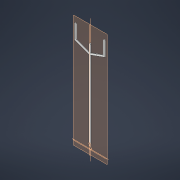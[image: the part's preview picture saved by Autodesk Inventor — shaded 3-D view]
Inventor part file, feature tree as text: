
AUTODESK INVENTOR PART (.ipt)
format: ipt  version: 2021 (Build 250183000, 183)  size: 134,656 bytes
history: native  units: mm
features: extrude x2, sketch x2, mirror x1, plane x1
ambient origin geometry x8: Origin, YZ Plane, XZ Plane, XY Plane, X Axis, Y Axis, Z Axis, Center Point
bodies: Solid1 (feature_tree)
feature tree (6):
  extrude  "Extrusion1"  Depth=4.0mm
  mirror  "Mirror1"
  plane  "Work Plane1"
  extrude  "Extrusion2"  Depth=2.0mm TaperAngle=0.0deg
  sketch  "Sketch1"  dims[d6=15.0mm d7=4.0mm]
  sketch  "Sketch3"  dims[d12=4.0mm d16=2.0mm d17=0.0mm d19=2.0mm d20=270.0mm d22=135.0deg d23=2.0mm d24=12.217305mm d26=2.0mm d27=40.0mm d28=135.0deg d31=35.0mm d32=20.0mm d33=0.0mm d34=0.0mm]
